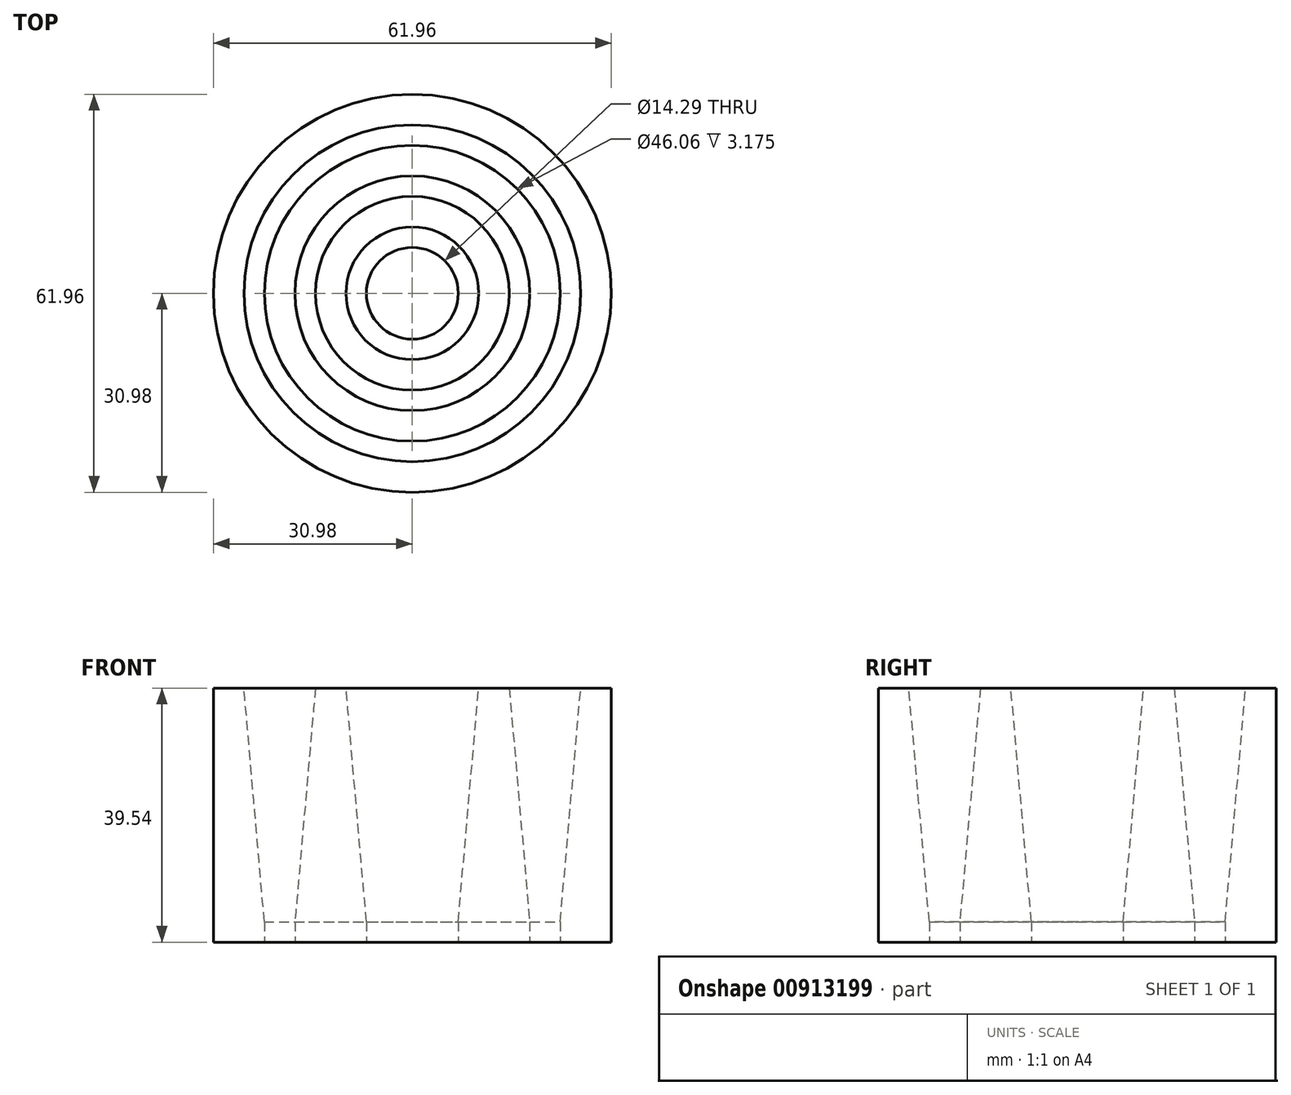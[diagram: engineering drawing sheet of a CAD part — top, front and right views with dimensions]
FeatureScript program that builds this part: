
annotation { "Feature Type Name" : "Feature", "Feature Type Description" : "" }
export const myFeature = defineFeature(function(context is Context, id is Id, definition is map)
    precondition{}
    {
        {
            var Q0;
            Q0=qCreatedBy(makeId("Front.planeOp"),FACE);
            var sketch = newSketch(context, id + "F0", { "sketchPlane" : qUnion([Q0])});
            skLineSegment(sketch, "E0", {"start": v(0, -14.34) * mm, "end": v(0, 49.43) * mm, "construction": true});
            skLineSegment(sketch, "E1", {"start": v(0, 6.35) * mm, "end": v(7.14, 6.35) * mm});
            skLineSegment(sketch, "E2", {"start": v(7.14, 6.35) * mm, "end": v(10.33, 42.71) * mm});
            skLineSegment(sketch, "E3", {"start": v(10.33, 42.71) * mm, "end": v(15.09, 42.71) * mm});
            skLineSegment(sketch, "E4", {"start": v(15.09, 42.71) * mm, "end": v(18.27, 6.35) * mm});
            skLineSegment(sketch, "E5", {"start": v(18.27, 6.35) * mm, "end": v(23.03, 6.35) * mm});
            skLineSegment(sketch, "E6", {"start": v(23.03, 6.35) * mm, "end": v(26.21, 42.71) * mm});
            skLineSegment(sketch, "E7", {"start": v(26.21, 42.71) * mm, "end": v(30.98, 42.71) * mm});
            skLineSegment(sketch, "E8", {"start": v(30.98, 42.71) * mm, "end": v(30.98, 0) * mm});
            skLineSegment(sketch, "E9", {"start": v(30.98, 0) * mm, "end": v(0, 0) * mm});
            skLineSegment(sketch, "E10", {"start": v(0, 0) * mm, "end": v(0, 6.35) * mm});
            skLineSegment(sketch, "E11", {"start": v(7.14, 6.35) * mm, "end": v(7.14, 3.17) * mm});
            skLineSegment(sketch, "E12", {"start": v(7.14, 3.17) * mm, "end": v(18.27, 3.17) * mm});
            skLineSegment(sketch, "E13", {"start": v(18.27, 3.17) * mm, "end": v(18.27, 6.35) * mm});
            skLineSegment(sketch, "E14", {"start": v(23.03, 6.35) * mm, "end": v(23.03, 3.18) * mm});
            skLineSegment(sketch, "E15", {"start": v(23.03, 3.18) * mm, "end": v(30.98, 3.18) * mm});
            skSolve(sketch);
        }
        {
            var Q0;
            Q0=makeQuery(id+"F0.imprint","IMPRINT",FACE,{"disambiguationData":[TD([[makeQuery(id+"F0.imprint","IMPRINT",EDGE,{"derivedFrom":sQuery(id+"F0.wireOp",EDGE,"E2")}),-1.0]])]});
            var Q1;
            Q1=makeQuery(id+"F0.imprint","IMPRINT",FACE,{"disambiguationData":[TD([[makeQuery(id+"F0.imprint","IMPRINT",EDGE,{"derivedFrom":sQuery(id+"F0.wireOp",EDGE,"E6")}),-1.0]])]});
            var Q2;
            Q2=sQuery(id+"F0.wireOp",EDGE,"E0");
            revolve(context, id + "F1", {"surfaceOperationType" : NewSurfaceOperationType.NEW, "entities" : qUnion([Q0, Q1]), "axis" : qUnion([Q2]), "revolveType" : RevolveType.FULL});
        }
    });
